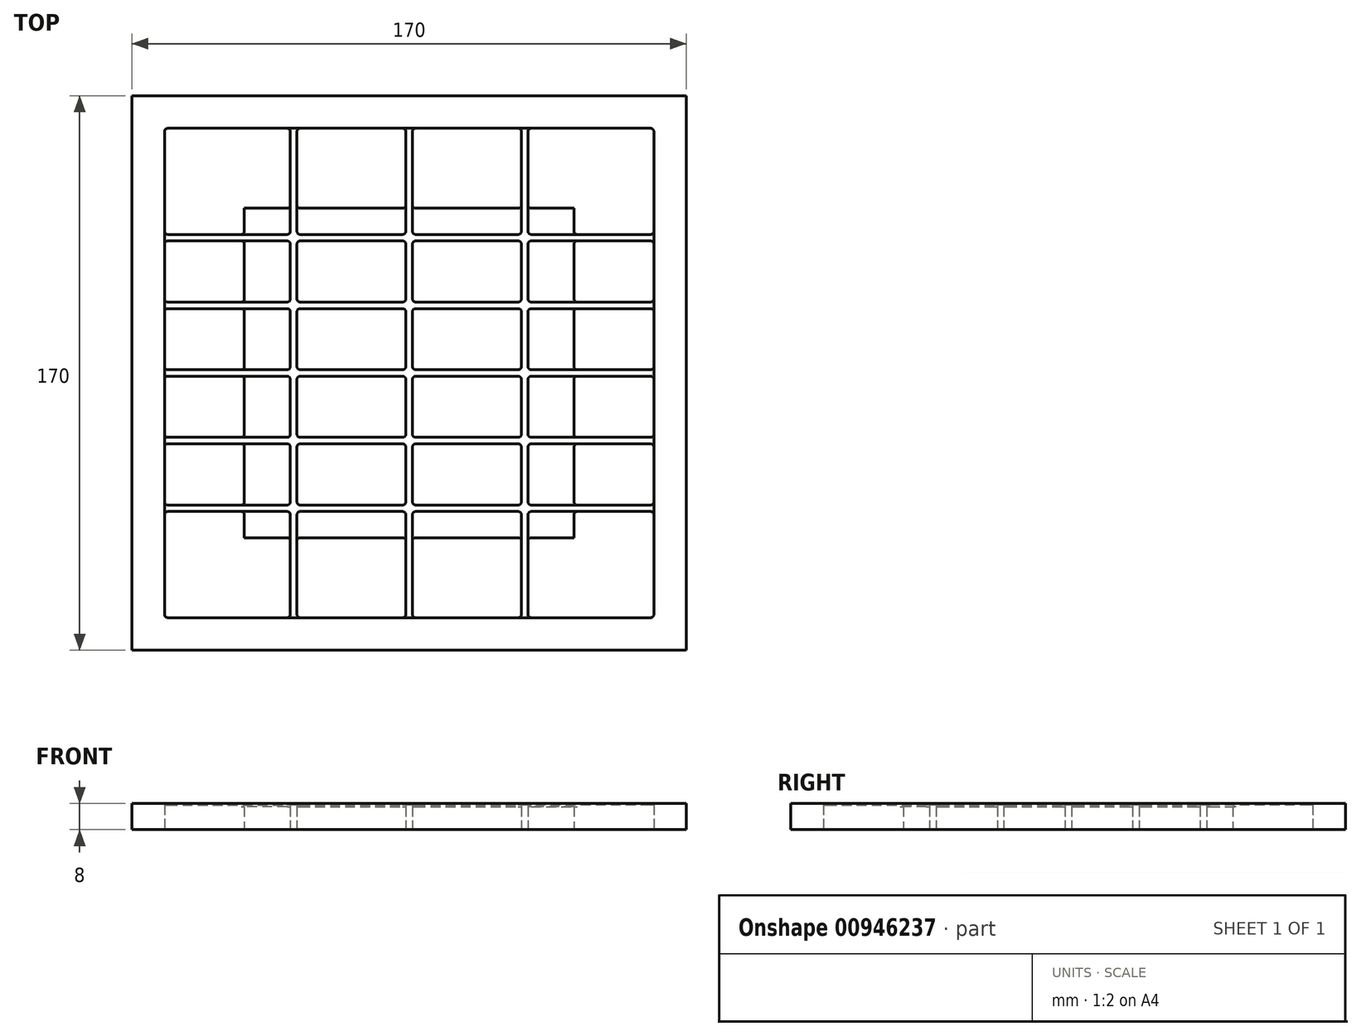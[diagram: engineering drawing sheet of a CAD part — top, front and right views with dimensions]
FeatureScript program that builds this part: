
annotation { "Feature Type Name" : "Feature", "Feature Type Description" : "" }
export const myFeature = defineFeature(function(context is Context, id is Id, definition is map)
    precondition{}
    {
        {
            var Q0;
            Q0=qCreatedBy(makeId("Top.planeOp"),FACE);
            var sketch = newSketch(context, id + "F0", { "sketchPlane" : qUnion([Q0])});
            skLineSegment(sketch, "E0", {"start": v(-85, -85) * mm, "end": v(-85, 85) * mm});
            skLineSegment(sketch, "E1", {"start": v(-85, 85) * mm, "end": v(85, 85) * mm});
            skLineSegment(sketch, "E2", {"start": v(85, 85) * mm, "end": v(85, -85) * mm});
            skLineSegment(sketch, "E3", {"start": v(85, -85) * mm, "end": v(-85, -85) * mm});
            skLineSegment(sketch, "E4", {"start": v(-2, -21.74) * mm, "end": v(-33.4, -21.74) * mm});
            skArc(sketch, "E5", {"start": v(-33.4, -21.74) * mm, "mid": v(-34.12, -22.03) * mm, "end": v(-34.4, -22.74) * mm});
            skLineSegment(sketch, "E6", {"start": v(-34.4, -22.74) * mm, "end": v(-34.4, -39.47) * mm});
            skArc(sketch, "E7", {"start": v(-34.4, -39.47) * mm, "mid": v(-34.12, -40.18) * mm, "end": v(-33.4, -40.47) * mm});
            skLineSegment(sketch, "E8", {"start": v(-33.4, -40.47) * mm, "end": v(-2, -40.47) * mm});
            skArc(sketch, "E9", {"start": v(-2, -40.47) * mm, "mid": v(-1.3, -40.18) * mm, "end": v(-1, -39.47) * mm});
            skLineSegment(sketch, "E10", {"start": v(-1, -39.47) * mm, "end": v(-1, -22.74) * mm});
            skArc(sketch, "E11", {"start": v(-1, -22.74) * mm, "mid": v(-1.3, -22.03) * mm, "end": v(-2, -21.74) * mm});
            skLineSegment(sketch, "E12", {"start": v(-2, 40.47) * mm, "end": v(-33.4, 40.47) * mm});
            skArc(sketch, "E13", {"start": v(-33.4, 40.47) * mm, "mid": v(-34.12, 40.18) * mm, "end": v(-34.4, 39.47) * mm});
            skLineSegment(sketch, "E14", {"start": v(-34.4, 39.47) * mm, "end": v(-34.4, 22.73) * mm});
            skArc(sketch, "E15", {"start": v(-34.4, 22.73) * mm, "mid": v(-34.12, 22.03) * mm, "end": v(-33.4, 21.73) * mm});
            skLineSegment(sketch, "E16", {"start": v(-33.4, 21.73) * mm, "end": v(-2, 21.73) * mm});
            skArc(sketch, "E17", {"start": v(-2, 21.73) * mm, "mid": v(-1.3, 22.03) * mm, "end": v(-1, 22.73) * mm});
            skLineSegment(sketch, "E18", {"start": v(-1, 22.73) * mm, "end": v(-1, 39.47) * mm});
            skArc(sketch, "E19", {"start": v(-1, 39.47) * mm, "mid": v(-1.3, 40.18) * mm, "end": v(-2, 40.47) * mm});
            skArc(sketch, "E20", {"start": v(1, 22.73) * mm, "mid": v(1.3, 22.03) * mm, "end": v(2, 21.73) * mm});
            skLineSegment(sketch, "E21", {"start": v(2, 21.73) * mm, "end": v(33.4, 21.73) * mm});
            skArc(sketch, "E22", {"start": v(33.4, 21.73) * mm, "mid": v(34.12, 22.03) * mm, "end": v(34.4, 22.73) * mm});
            skLineSegment(sketch, "E23", {"start": v(34.4, 22.73) * mm, "end": v(34.4, 39.47) * mm});
            skArc(sketch, "E24", {"start": v(34.4, 39.47) * mm, "mid": v(34.12, 40.18) * mm, "end": v(33.4, 40.47) * mm});
            skLineSegment(sketch, "E25", {"start": v(33.4, 40.47) * mm, "end": v(2, 40.47) * mm});
            skArc(sketch, "E26", {"start": v(2, 40.47) * mm, "mid": v(1.3, 40.18) * mm, "end": v(1, 39.47) * mm});
            skLineSegment(sketch, "E27", {"start": v(1, 39.47) * mm, "end": v(1, 22.73) * mm});
            skLineSegment(sketch, "E28", {"start": v(-33.4, 1) * mm, "end": v(-2, 1) * mm});
            skArc(sketch, "E29", {"start": v(-2, 1) * mm, "mid": v(-1.3, 1.3) * mm, "end": v(-1, 2) * mm});
            skLineSegment(sketch, "E30", {"start": v(-1, 2) * mm, "end": v(-1, 18.73) * mm});
            skArc(sketch, "E31", {"start": v(-1, 18.73) * mm, "mid": v(-1.3, 19.44) * mm, "end": v(-2, 19.73) * mm});
            skLineSegment(sketch, "E32", {"start": v(-2, 19.73) * mm, "end": v(-33.4, 19.73) * mm});
            skArc(sketch, "E33", {"start": v(-33.4, 19.73) * mm, "mid": v(-34.12, 19.44) * mm, "end": v(-34.4, 18.73) * mm});
            skLineSegment(sketch, "E34", {"start": v(-34.4, 18.73) * mm, "end": v(-34.4, 2) * mm});
            skArc(sketch, "E35", {"start": v(-34.4, 2) * mm, "mid": v(-34.12, 1.3) * mm, "end": v(-33.4, 1) * mm});
            skLineSegment(sketch, "E36", {"start": v(2, 1) * mm, "end": v(33.4, 1) * mm});
            skArc(sketch, "E37", {"start": v(33.4, 1) * mm, "mid": v(34.12, 1.3) * mm, "end": v(34.4, 2) * mm});
            skLineSegment(sketch, "E38", {"start": v(34.4, 2) * mm, "end": v(34.4, 18.73) * mm});
            skArc(sketch, "E39", {"start": v(34.4, 18.73) * mm, "mid": v(34.12, 19.44) * mm, "end": v(33.4, 19.73) * mm});
            skLineSegment(sketch, "E40", {"start": v(33.4, 19.73) * mm, "end": v(2, 19.73) * mm});
            skArc(sketch, "E41", {"start": v(2, 19.73) * mm, "mid": v(1.3, 19.44) * mm, "end": v(1, 18.73) * mm});
            skLineSegment(sketch, "E42", {"start": v(1, 18.73) * mm, "end": v(1, 2) * mm});
            skArc(sketch, "E43", {"start": v(1, 2) * mm, "mid": v(1.3, 1.3) * mm, "end": v(2, 1) * mm});
            skArc(sketch, "E44", {"start": v(33.4, -19.74) * mm, "mid": v(34.12, -19.44) * mm, "end": v(34.4, -18.74) * mm});
            skLineSegment(sketch, "E45", {"start": v(34.4, -18.74) * mm, "end": v(34.4, -2) * mm});
            skArc(sketch, "E46", {"start": v(34.4, -2) * mm, "mid": v(34.12, -1.3) * mm, "end": v(33.4, -1) * mm});
            skLineSegment(sketch, "E47", {"start": v(33.4, -1) * mm, "end": v(2, -1) * mm});
            skArc(sketch, "E48", {"start": v(2, -1) * mm, "mid": v(1.3, -1.3) * mm, "end": v(1, -2) * mm});
            skLineSegment(sketch, "E49", {"start": v(1, -2) * mm, "end": v(1, -18.74) * mm});
            skArc(sketch, "E50", {"start": v(1, -18.74) * mm, "mid": v(1.3, -19.44) * mm, "end": v(2, -19.74) * mm});
            skLineSegment(sketch, "E51", {"start": v(2, -19.74) * mm, "end": v(33.4, -19.74) * mm});
            skLineSegment(sketch, "E52", {"start": v(-1, -18.74) * mm, "end": v(-1, -2) * mm});
            skArc(sketch, "E53", {"start": v(-1, -2) * mm, "mid": v(-1.3, -1.3) * mm, "end": v(-2, -1) * mm});
            skLineSegment(sketch, "E54", {"start": v(-2, -1) * mm, "end": v(-33.4, -1) * mm});
            skArc(sketch, "E55", {"start": v(-33.4, -1) * mm, "mid": v(-34.12, -1.3) * mm, "end": v(-34.4, -2) * mm});
            skLineSegment(sketch, "E56", {"start": v(-34.4, -2) * mm, "end": v(-34.4, -18.74) * mm});
            skArc(sketch, "E57", {"start": v(-34.4, -18.74) * mm, "mid": v(-34.12, -19.44) * mm, "end": v(-33.4, -19.74) * mm});
            skLineSegment(sketch, "E58", {"start": v(-33.4, -19.74) * mm, "end": v(-2, -19.74) * mm});
            skArc(sketch, "E59", {"start": v(-2, -19.74) * mm, "mid": v(-1.3, -19.44) * mm, "end": v(-1, -18.74) * mm});
            skArc(sketch, "E60", {"start": v(2, -21.74) * mm, "mid": v(1.3, -22.03) * mm, "end": v(1, -22.74) * mm});
            skLineSegment(sketch, "E61", {"start": v(1, -22.74) * mm, "end": v(1, -39.47) * mm});
            skArc(sketch, "E62", {"start": v(1, -39.47) * mm, "mid": v(1.3, -40.18) * mm, "end": v(2, -40.47) * mm});
            skLineSegment(sketch, "E63", {"start": v(2, -40.47) * mm, "end": v(33.4, -40.47) * mm});
            skArc(sketch, "E64", {"start": v(33.4, -40.47) * mm, "mid": v(34.12, -40.18) * mm, "end": v(34.4, -39.47) * mm});
            skLineSegment(sketch, "E65", {"start": v(34.4, -39.47) * mm, "end": v(34.4, -22.74) * mm});
            skArc(sketch, "E66", {"start": v(34.4, -22.74) * mm, "mid": v(34.12, -22.03) * mm, "end": v(33.4, -21.74) * mm});
            skLineSegment(sketch, "E67", {"start": v(33.4, -21.74) * mm, "end": v(2, -21.74) * mm});
            skLineSegment(sketch, "E68", {"start": v(36.4, 50.5) * mm, "end": v(36.4, 43.47) * mm});
            skArc(sketch, "E69", {"start": v(36.4, 43.47) * mm, "mid": v(36.7, 42.76) * mm, "end": v(37.4, 42.47) * mm});
            skLineSegment(sketch, "E70", {"start": v(37.4, 42.47) * mm, "end": v(50.5, 42.47) * mm});
            skLineSegment(sketch, "E71", {"start": v(50.5, 42.47) * mm, "end": v(50.5, 50.5) * mm});
            skLineSegment(sketch, "E72", {"start": v(50.5, 50.5) * mm, "end": v(36.4, 50.5) * mm});
            skLineSegment(sketch, "E73", {"start": v(1, 50.5) * mm, "end": v(1, 43.47) * mm});
            skArc(sketch, "E74", {"start": v(1, 43.47) * mm, "mid": v(1.3, 42.76) * mm, "end": v(2, 42.47) * mm});
            skLineSegment(sketch, "E75", {"start": v(2, 42.47) * mm, "end": v(33.4, 42.47) * mm});
            skArc(sketch, "E76", {"start": v(33.4, 42.47) * mm, "mid": v(34.12, 42.76) * mm, "end": v(34.4, 43.47) * mm});
            skLineSegment(sketch, "E77", {"start": v(34.4, 43.47) * mm, "end": v(34.4, 50.5) * mm});
            skLineSegment(sketch, "E78", {"start": v(34.4, 50.5) * mm, "end": v(1, 50.5) * mm});
            skLineSegment(sketch, "E79", {"start": v(-34.4, 50.5) * mm, "end": v(-34.4, 43.47) * mm});
            skArc(sketch, "E80", {"start": v(-34.4, 43.47) * mm, "mid": v(-34.12, 42.76) * mm, "end": v(-33.4, 42.47) * mm});
            skLineSegment(sketch, "E81", {"start": v(-33.4, 42.47) * mm, "end": v(-2, 42.47) * mm});
            skArc(sketch, "E82", {"start": v(-2, 42.47) * mm, "mid": v(-1.3, 42.76) * mm, "end": v(-1, 43.47) * mm});
            skLineSegment(sketch, "E83", {"start": v(-1, 43.47) * mm, "end": v(-1, 50.5) * mm});
            skLineSegment(sketch, "E84", {"start": v(-1, 50.5) * mm, "end": v(-34.4, 50.5) * mm});
            skLineSegment(sketch, "E85", {"start": v(-50.5, -40.47) * mm, "end": v(-37.4, -40.47) * mm});
            skArc(sketch, "E86", {"start": v(-37.4, -40.47) * mm, "mid": v(-36.7, -40.18) * mm, "end": v(-36.4, -39.47) * mm});
            skLineSegment(sketch, "E87", {"start": v(-36.4, -39.47) * mm, "end": v(-36.4, -22.74) * mm});
            skArc(sketch, "E88", {"start": v(-36.4, -22.74) * mm, "mid": v(-36.7, -22.03) * mm, "end": v(-37.4, -21.74) * mm});
            skLineSegment(sketch, "E89", {"start": v(-37.4, -21.74) * mm, "end": v(-50.5, -21.74) * mm});
            skLineSegment(sketch, "E90", {"start": v(-50.5, -21.74) * mm, "end": v(-50.5, -40.47) * mm});
            skLineSegment(sketch, "E91", {"start": v(-50.5, -19.74) * mm, "end": v(-37.4, -19.74) * mm});
            skArc(sketch, "E92", {"start": v(-37.4, -19.74) * mm, "mid": v(-36.7, -19.44) * mm, "end": v(-36.4, -18.74) * mm});
            skLineSegment(sketch, "E93", {"start": v(-36.4, -18.74) * mm, "end": v(-36.4, -2) * mm});
            skArc(sketch, "E94", {"start": v(-36.4, -2) * mm, "mid": v(-36.7, -1.3) * mm, "end": v(-37.4, -1) * mm});
            skLineSegment(sketch, "E95", {"start": v(-37.4, -1) * mm, "end": v(-50.5, -1) * mm});
            skLineSegment(sketch, "E96", {"start": v(-50.5, -1) * mm, "end": v(-50.5, -19.74) * mm});
            skLineSegment(sketch, "E97", {"start": v(-50.5, 1) * mm, "end": v(-37.4, 1) * mm});
            skArc(sketch, "E98", {"start": v(-37.4, 1) * mm, "mid": v(-36.7, 1.3) * mm, "end": v(-36.4, 2) * mm});
            skLineSegment(sketch, "E99", {"start": v(-36.4, 2) * mm, "end": v(-36.4, 18.73) * mm});
            skArc(sketch, "E100", {"start": v(-36.4, 18.73) * mm, "mid": v(-36.7, 19.44) * mm, "end": v(-37.4, 19.73) * mm});
            skLineSegment(sketch, "E101", {"start": v(-37.4, 19.73) * mm, "end": v(-50.5, 19.73) * mm});
            skLineSegment(sketch, "E102", {"start": v(-50.5, 19.73) * mm, "end": v(-50.5, 1) * mm});
            skLineSegment(sketch, "E103", {"start": v(-50.5, 21.73) * mm, "end": v(-37.4, 21.73) * mm});
            skArc(sketch, "E104", {"start": v(-37.4, 21.73) * mm, "mid": v(-36.7, 22.03) * mm, "end": v(-36.4, 22.73) * mm});
            skLineSegment(sketch, "E105", {"start": v(-36.4, 22.73) * mm, "end": v(-36.4, 39.47) * mm});
            skArc(sketch, "E106", {"start": v(-36.4, 39.47) * mm, "mid": v(-36.7, 40.18) * mm, "end": v(-37.4, 40.47) * mm});
            skLineSegment(sketch, "E107", {"start": v(-37.4, 40.47) * mm, "end": v(-50.5, 40.47) * mm});
            skLineSegment(sketch, "E108", {"start": v(-50.5, 40.47) * mm, "end": v(-50.5, 21.73) * mm});
            skLineSegment(sketch, "E109", {"start": v(-50.5, 42.47) * mm, "end": v(-37.4, 42.47) * mm});
            skArc(sketch, "E110", {"start": v(-37.4, 42.47) * mm, "mid": v(-36.7, 42.76) * mm, "end": v(-36.4, 43.47) * mm});
            skLineSegment(sketch, "E111", {"start": v(-36.4, 43.47) * mm, "end": v(-36.4, 50.5) * mm});
            skLineSegment(sketch, "E112", {"start": v(-36.4, 50.5) * mm, "end": v(-50.5, 50.5) * mm});
            skLineSegment(sketch, "E113", {"start": v(-50.5, 50.5) * mm, "end": v(-50.5, 42.47) * mm});
            skLineSegment(sketch, "E114", {"start": v(34.4, -50.5) * mm, "end": v(34.4, -43.47) * mm});
            skArc(sketch, "E115", {"start": v(34.4, -43.47) * mm, "mid": v(34.12, -42.76) * mm, "end": v(33.4, -42.47) * mm});
            skLineSegment(sketch, "E116", {"start": v(33.4, -42.47) * mm, "end": v(2, -42.47) * mm});
            skArc(sketch, "E117", {"start": v(2, -42.47) * mm, "mid": v(1.3, -42.76) * mm, "end": v(1, -43.47) * mm});
            skLineSegment(sketch, "E118", {"start": v(1, -43.47) * mm, "end": v(1, -50.5) * mm});
            skLineSegment(sketch, "E119", {"start": v(1, -50.5) * mm, "end": v(34.4, -50.5) * mm});
            skLineSegment(sketch, "E120", {"start": v(-1, -50.5) * mm, "end": v(-1, -43.47) * mm});
            skArc(sketch, "E121", {"start": v(-1, -43.47) * mm, "mid": v(-1.3, -42.76) * mm, "end": v(-2, -42.47) * mm});
            skLineSegment(sketch, "E122", {"start": v(-2, -42.47) * mm, "end": v(-33.4, -42.47) * mm});
            skArc(sketch, "E123", {"start": v(-33.4, -42.47) * mm, "mid": v(-34.12, -42.76) * mm, "end": v(-34.4, -43.47) * mm});
            skLineSegment(sketch, "E124", {"start": v(-34.4, -43.47) * mm, "end": v(-34.4, -50.5) * mm});
            skLineSegment(sketch, "E125", {"start": v(-34.4, -50.5) * mm, "end": v(-1, -50.5) * mm});
            skLineSegment(sketch, "E126", {"start": v(-36.4, -50.5) * mm, "end": v(-36.4, -43.47) * mm});
            skArc(sketch, "E127", {"start": v(-36.4, -43.47) * mm, "mid": v(-36.7, -42.76) * mm, "end": v(-37.4, -42.47) * mm});
            skLineSegment(sketch, "E128", {"start": v(-37.4, -42.47) * mm, "end": v(-50.5, -42.47) * mm});
            skLineSegment(sketch, "E129", {"start": v(-50.5, -42.47) * mm, "end": v(-50.5, -50.5) * mm});
            skLineSegment(sketch, "E130", {"start": v(-50.5, -50.5) * mm, "end": v(-36.4, -50.5) * mm});
            skLineSegment(sketch, "E131", {"start": v(50.5, -42.47) * mm, "end": v(37.4, -42.47) * mm});
            skArc(sketch, "E132", {"start": v(37.4, -42.47) * mm, "mid": v(36.7, -42.76) * mm, "end": v(36.4, -43.47) * mm});
            skLineSegment(sketch, "E133", {"start": v(36.4, -43.47) * mm, "end": v(36.4, -50.5) * mm});
            skLineSegment(sketch, "E134", {"start": v(36.4, -50.5) * mm, "end": v(50.5, -50.5) * mm});
            skLineSegment(sketch, "E135", {"start": v(50.5, -50.5) * mm, "end": v(50.5, -42.47) * mm});
            skLineSegment(sketch, "E136", {"start": v(50.5, -21.74) * mm, "end": v(37.4, -21.74) * mm});
            skArc(sketch, "E137", {"start": v(37.4, -21.74) * mm, "mid": v(36.7, -22.03) * mm, "end": v(36.4, -22.74) * mm});
            skLineSegment(sketch, "E138", {"start": v(36.4, -22.74) * mm, "end": v(36.4, -39.47) * mm});
            skArc(sketch, "E139", {"start": v(36.4, -39.47) * mm, "mid": v(36.7, -40.18) * mm, "end": v(37.4, -40.47) * mm});
            skLineSegment(sketch, "E140", {"start": v(37.4, -40.47) * mm, "end": v(50.5, -40.47) * mm});
            skLineSegment(sketch, "E141", {"start": v(50.5, -40.47) * mm, "end": v(50.5, -21.74) * mm});
            skLineSegment(sketch, "E142", {"start": v(50.5, -1) * mm, "end": v(37.4, -1) * mm});
            skArc(sketch, "E143", {"start": v(37.4, -1) * mm, "mid": v(36.7, -1.3) * mm, "end": v(36.4, -2) * mm});
            skLineSegment(sketch, "E144", {"start": v(36.4, -2) * mm, "end": v(36.4, -18.74) * mm});
            skArc(sketch, "E145", {"start": v(36.4, -18.74) * mm, "mid": v(36.7, -19.44) * mm, "end": v(37.4, -19.74) * mm});
            skLineSegment(sketch, "E146", {"start": v(37.4, -19.74) * mm, "end": v(50.5, -19.74) * mm});
            skLineSegment(sketch, "E147", {"start": v(50.5, -19.74) * mm, "end": v(50.5, -1) * mm});
            skLineSegment(sketch, "E148", {"start": v(50.5, 19.73) * mm, "end": v(37.4, 19.73) * mm});
            skArc(sketch, "E149", {"start": v(37.4, 19.73) * mm, "mid": v(36.7, 19.44) * mm, "end": v(36.4, 18.73) * mm});
            skLineSegment(sketch, "E150", {"start": v(36.4, 18.73) * mm, "end": v(36.4, 2) * mm});
            skArc(sketch, "E151", {"start": v(36.4, 2) * mm, "mid": v(36.7, 1.3) * mm, "end": v(37.4, 1) * mm});
            skLineSegment(sketch, "E152", {"start": v(37.4, 1) * mm, "end": v(50.5, 1) * mm});
            skLineSegment(sketch, "E153", {"start": v(50.5, 1) * mm, "end": v(50.5, 19.73) * mm});
            skLineSegment(sketch, "E154", {"start": v(50.5, 40.47) * mm, "end": v(37.4, 40.47) * mm});
            skArc(sketch, "E155", {"start": v(37.4, 40.47) * mm, "mid": v(36.7, 40.18) * mm, "end": v(36.4, 39.47) * mm});
            skLineSegment(sketch, "E156", {"start": v(36.4, 39.47) * mm, "end": v(36.4, 22.73) * mm});
            skArc(sketch, "E157", {"start": v(36.4, 22.73) * mm, "mid": v(36.7, 22.03) * mm, "end": v(37.4, 21.73) * mm});
            skLineSegment(sketch, "E158", {"start": v(37.4, 21.73) * mm, "end": v(50.5, 21.73) * mm});
            skLineSegment(sketch, "E159", {"start": v(50.5, 21.73) * mm, "end": v(50.5, 40.47) * mm});
            skArc(sketch, "E160", {"start": v(75, 2) * mm, "mid": v(74.7, 1.3) * mm, "end": v(74, 1) * mm});
            skLineSegment(sketch, "E161", {"start": v(74, 1) * mm, "end": v(37.4, 1) * mm});
            skArc(sketch, "E162", {"start": v(37.4, 1) * mm, "mid": v(36.7, 1.3) * mm, "end": v(36.4, 2) * mm});
            skLineSegment(sketch, "E163", {"start": v(36.4, 2) * mm, "end": v(36.4, 18.73) * mm});
            skArc(sketch, "E164", {"start": v(36.4, 18.73) * mm, "mid": v(36.7, 19.44) * mm, "end": v(37.4, 19.73) * mm});
            skLineSegment(sketch, "E165", {"start": v(37.4, 19.73) * mm, "end": v(74, 19.73) * mm});
            skArc(sketch, "E166", {"start": v(74, 19.73) * mm, "mid": v(74.7, 19.44) * mm, "end": v(75, 18.73) * mm});
            skLineSegment(sketch, "E167", {"start": v(75, 18.73) * mm, "end": v(75, 22.73) * mm});
            skArc(sketch, "E168", {"start": v(75, 22.73) * mm, "mid": v(74.7, 22.03) * mm, "end": v(74, 21.73) * mm});
            skLineSegment(sketch, "E169", {"start": v(74, 21.73) * mm, "end": v(37.4, 21.73) * mm});
            skArc(sketch, "E170", {"start": v(37.4, 21.73) * mm, "mid": v(36.7, 22.03) * mm, "end": v(36.4, 22.73) * mm});
            skLineSegment(sketch, "E171", {"start": v(36.4, 22.73) * mm, "end": v(36.4, 39.47) * mm});
            skArc(sketch, "E172", {"start": v(36.4, 39.47) * mm, "mid": v(36.7, 40.18) * mm, "end": v(37.4, 40.47) * mm});
            skLineSegment(sketch, "E173", {"start": v(37.4, 40.47) * mm, "end": v(74, 40.47) * mm});
            skArc(sketch, "E174", {"start": v(74, 40.47) * mm, "mid": v(74.7, 40.18) * mm, "end": v(75, 39.47) * mm});
            skLineSegment(sketch, "E175", {"start": v(75, 39.47) * mm, "end": v(75, 43.47) * mm});
            skArc(sketch, "E176", {"start": v(75, 43.47) * mm, "mid": v(74.7, 42.76) * mm, "end": v(74, 42.47) * mm});
            skLineSegment(sketch, "E177", {"start": v(74, 42.47) * mm, "end": v(37.4, 42.47) * mm});
            skArc(sketch, "E178", {"start": v(37.4, 42.47) * mm, "mid": v(36.7, 42.76) * mm, "end": v(36.4, 43.47) * mm});
            skLineSegment(sketch, "E179", {"start": v(36.4, 43.47) * mm, "end": v(36.4, 74) * mm});
            skArc(sketch, "E180", {"start": v(36.4, 74) * mm, "mid": v(36.7, 74.7) * mm, "end": v(37.4, 75) * mm});
            skLineSegment(sketch, "E181", {"start": v(37.4, 75) * mm, "end": v(33.4, 75) * mm});
            skArc(sketch, "E182", {"start": v(33.4, 75) * mm, "mid": v(34.12, 74.7) * mm, "end": v(34.4, 74) * mm});
            skLineSegment(sketch, "E183", {"start": v(34.4, 74) * mm, "end": v(34.4, 43.47) * mm});
            skArc(sketch, "E184", {"start": v(34.4, 43.47) * mm, "mid": v(34.12, 42.76) * mm, "end": v(33.4, 42.47) * mm});
            skLineSegment(sketch, "E185", {"start": v(33.4, 42.47) * mm, "end": v(2, 42.47) * mm});
            skArc(sketch, "E186", {"start": v(2, 42.47) * mm, "mid": v(1.3, 42.76) * mm, "end": v(1, 43.47) * mm});
            skLineSegment(sketch, "E187", {"start": v(1, 43.47) * mm, "end": v(1, 74) * mm});
            skArc(sketch, "E188", {"start": v(1, 74) * mm, "mid": v(1.3, 74.7) * mm, "end": v(2, 75) * mm});
            skLineSegment(sketch, "E189", {"start": v(2, 75) * mm, "end": v(-2, 75) * mm});
            skArc(sketch, "E190", {"start": v(-2, 75) * mm, "mid": v(-1.3, 74.7) * mm, "end": v(-1, 74) * mm});
            skLineSegment(sketch, "E191", {"start": v(-1, 74) * mm, "end": v(-1, 43.47) * mm});
            skArc(sketch, "E192", {"start": v(-1, 43.47) * mm, "mid": v(-1.3, 42.76) * mm, "end": v(-2, 42.47) * mm});
            skLineSegment(sketch, "E193", {"start": v(-2, 42.47) * mm, "end": v(-33.4, 42.47) * mm});
            skArc(sketch, "E194", {"start": v(-33.4, 42.47) * mm, "mid": v(-34.12, 42.76) * mm, "end": v(-34.4, 43.47) * mm});
            skLineSegment(sketch, "E195", {"start": v(-34.4, 43.47) * mm, "end": v(-34.4, 74) * mm});
            skArc(sketch, "E196", {"start": v(-34.4, 74) * mm, "mid": v(-34.12, 74.7) * mm, "end": v(-33.4, 75) * mm});
            skLineSegment(sketch, "E197", {"start": v(-33.4, 75) * mm, "end": v(-37.4, 75) * mm});
            skArc(sketch, "E198", {"start": v(-37.4, 75) * mm, "mid": v(-36.7, 74.7) * mm, "end": v(-36.4, 74) * mm});
            skLineSegment(sketch, "E199", {"start": v(-36.4, 74) * mm, "end": v(-36.4, 43.47) * mm});
            skArc(sketch, "E200", {"start": v(-36.4, 43.47) * mm, "mid": v(-36.7, 42.76) * mm, "end": v(-37.4, 42.47) * mm});
            skLineSegment(sketch, "E201", {"start": v(-37.4, 42.47) * mm, "end": v(-74, 42.47) * mm});
            skArc(sketch, "E202", {"start": v(-74, 42.47) * mm, "mid": v(-74.7, 42.76) * mm, "end": v(-75, 43.47) * mm});
            skLineSegment(sketch, "E203", {"start": v(-75, 43.47) * mm, "end": v(-75, 39.47) * mm});
            skArc(sketch, "E204", {"start": v(-75, 39.47) * mm, "mid": v(-74.7, 40.18) * mm, "end": v(-74, 40.47) * mm});
            skLineSegment(sketch, "E205", {"start": v(-74, 40.47) * mm, "end": v(-37.4, 40.47) * mm});
            skArc(sketch, "E206", {"start": v(-37.4, 40.47) * mm, "mid": v(-36.7, 40.18) * mm, "end": v(-36.4, 39.47) * mm});
            skLineSegment(sketch, "E207", {"start": v(-36.4, 39.47) * mm, "end": v(-36.4, 22.73) * mm});
            skArc(sketch, "E208", {"start": v(-36.4, 22.73) * mm, "mid": v(-36.7, 22.03) * mm, "end": v(-37.4, 21.73) * mm});
            skLineSegment(sketch, "E209", {"start": v(-37.4, 21.73) * mm, "end": v(-74, 21.73) * mm});
            skArc(sketch, "E210", {"start": v(-74, 21.73) * mm, "mid": v(-74.7, 22.03) * mm, "end": v(-75, 22.73) * mm});
            skLineSegment(sketch, "E211", {"start": v(-75, 22.73) * mm, "end": v(-75, 18.73) * mm});
            skArc(sketch, "E212", {"start": v(-75, 18.73) * mm, "mid": v(-74.7, 19.44) * mm, "end": v(-74, 19.73) * mm});
            skLineSegment(sketch, "E213", {"start": v(-74, 19.73) * mm, "end": v(-37.4, 19.73) * mm});
            skArc(sketch, "E214", {"start": v(-37.4, 19.73) * mm, "mid": v(-36.7, 19.44) * mm, "end": v(-36.4, 18.73) * mm});
            skLineSegment(sketch, "E215", {"start": v(-36.4, 18.73) * mm, "end": v(-36.4, 2) * mm});
            skArc(sketch, "E216", {"start": v(-36.4, 2) * mm, "mid": v(-36.7, 1.3) * mm, "end": v(-37.4, 1) * mm});
            skLineSegment(sketch, "E217", {"start": v(-37.4, 1) * mm, "end": v(-74, 1) * mm});
            skArc(sketch, "E218", {"start": v(-74, 1) * mm, "mid": v(-74.7, 1.3) * mm, "end": v(-75, 2) * mm});
            skLineSegment(sketch, "E219", {"start": v(-75, 2) * mm, "end": v(-75, -2) * mm});
            skArc(sketch, "E220", {"start": v(-75, -2) * mm, "mid": v(-74.7, -1.3) * mm, "end": v(-74, -1) * mm});
            skLineSegment(sketch, "E221", {"start": v(-74, -1) * mm, "end": v(-37.4, -1) * mm});
            skArc(sketch, "E222", {"start": v(-37.4, -1) * mm, "mid": v(-36.7, -1.3) * mm, "end": v(-36.4, -2) * mm});
            skLineSegment(sketch, "E223", {"start": v(-36.4, -2) * mm, "end": v(-36.4, -18.74) * mm});
            skArc(sketch, "E224", {"start": v(-36.4, -18.74) * mm, "mid": v(-36.7, -19.44) * mm, "end": v(-37.4, -19.74) * mm});
            skLineSegment(sketch, "E225", {"start": v(-37.4, -19.74) * mm, "end": v(-74, -19.74) * mm});
            skArc(sketch, "E226", {"start": v(-74, -19.74) * mm, "mid": v(-74.7, -19.44) * mm, "end": v(-75, -18.74) * mm});
            skLineSegment(sketch, "E227", {"start": v(-75, -18.74) * mm, "end": v(-75, -22.74) * mm});
            skArc(sketch, "E228", {"start": v(-75, -22.74) * mm, "mid": v(-74.7, -22.03) * mm, "end": v(-74, -21.74) * mm});
            skLineSegment(sketch, "E229", {"start": v(-74, -21.74) * mm, "end": v(-37.4, -21.74) * mm});
            skArc(sketch, "E230", {"start": v(-37.4, -21.74) * mm, "mid": v(-36.7, -22.03) * mm, "end": v(-36.4, -22.74) * mm});
            skLineSegment(sketch, "E231", {"start": v(-36.4, -22.74) * mm, "end": v(-36.4, -39.47) * mm});
            skArc(sketch, "E232", {"start": v(-36.4, -39.47) * mm, "mid": v(-36.7, -40.18) * mm, "end": v(-37.4, -40.47) * mm});
            skLineSegment(sketch, "E233", {"start": v(-37.4, -40.47) * mm, "end": v(-74, -40.47) * mm});
            skArc(sketch, "E234", {"start": v(-74, -40.47) * mm, "mid": v(-74.7, -40.18) * mm, "end": v(-75, -39.47) * mm});
            skLineSegment(sketch, "E235", {"start": v(-75, -39.47) * mm, "end": v(-75, -43.47) * mm});
            skArc(sketch, "E236", {"start": v(-75, -43.47) * mm, "mid": v(-74.7, -42.76) * mm, "end": v(-74, -42.47) * mm});
            skLineSegment(sketch, "E237", {"start": v(-74, -42.47) * mm, "end": v(-37.4, -42.47) * mm});
            skArc(sketch, "E238", {"start": v(-37.4, -42.47) * mm, "mid": v(-36.7, -42.76) * mm, "end": v(-36.4, -43.47) * mm});
            skLineSegment(sketch, "E239", {"start": v(-36.4, -43.47) * mm, "end": v(-36.4, -74) * mm});
            skArc(sketch, "E240", {"start": v(-36.4, -74) * mm, "mid": v(-36.7, -74.7) * mm, "end": v(-37.4, -75) * mm});
            skLineSegment(sketch, "E241", {"start": v(-37.4, -75) * mm, "end": v(-33.4, -75) * mm});
            skArc(sketch, "E242", {"start": v(-33.4, -75) * mm, "mid": v(-34.12, -74.7) * mm, "end": v(-34.4, -74) * mm});
            skLineSegment(sketch, "E243", {"start": v(-34.4, -74) * mm, "end": v(-34.4, -43.47) * mm});
            skArc(sketch, "E244", {"start": v(-34.4, -43.47) * mm, "mid": v(-34.12, -42.76) * mm, "end": v(-33.4, -42.47) * mm});
            skLineSegment(sketch, "E245", {"start": v(-33.4, -42.47) * mm, "end": v(-2, -42.47) * mm});
            skArc(sketch, "E246", {"start": v(-2, -42.47) * mm, "mid": v(-1.3, -42.76) * mm, "end": v(-1, -43.47) * mm});
            skLineSegment(sketch, "E247", {"start": v(-1, -43.47) * mm, "end": v(-1, -74) * mm});
            skArc(sketch, "E248", {"start": v(-1, -74) * mm, "mid": v(-1.3, -74.7) * mm, "end": v(-2, -75) * mm});
            skLineSegment(sketch, "E249", {"start": v(-2, -75) * mm, "end": v(2, -75) * mm});
            skArc(sketch, "E250", {"start": v(2, -75) * mm, "mid": v(1.3, -74.7) * mm, "end": v(1, -74) * mm});
            skLineSegment(sketch, "E251", {"start": v(1, -74) * mm, "end": v(1, -43.47) * mm});
            skArc(sketch, "E252", {"start": v(1, -43.47) * mm, "mid": v(1.3, -42.76) * mm, "end": v(2, -42.47) * mm});
            skLineSegment(sketch, "E253", {"start": v(2, -42.47) * mm, "end": v(33.4, -42.47) * mm});
            skArc(sketch, "E254", {"start": v(33.4, -42.47) * mm, "mid": v(34.12, -42.76) * mm, "end": v(34.4, -43.47) * mm});
            skLineSegment(sketch, "E255", {"start": v(34.4, -43.47) * mm, "end": v(34.4, -74) * mm});
            skArc(sketch, "E256", {"start": v(34.4, -74) * mm, "mid": v(34.12, -74.7) * mm, "end": v(33.4, -75) * mm});
            skLineSegment(sketch, "E257", {"start": v(33.4, -75) * mm, "end": v(37.4, -75) * mm});
            skArc(sketch, "E258", {"start": v(37.4, -75) * mm, "mid": v(36.7, -74.7) * mm, "end": v(36.4, -74) * mm});
            skLineSegment(sketch, "E259", {"start": v(36.4, -74) * mm, "end": v(36.4, -43.47) * mm});
            skArc(sketch, "E260", {"start": v(36.4, -43.47) * mm, "mid": v(36.7, -42.76) * mm, "end": v(37.4, -42.47) * mm});
            skLineSegment(sketch, "E261", {"start": v(37.4, -42.47) * mm, "end": v(74, -42.47) * mm});
            skArc(sketch, "E262", {"start": v(74, -42.47) * mm, "mid": v(74.7, -42.76) * mm, "end": v(75, -43.47) * mm});
            skLineSegment(sketch, "E263", {"start": v(75, -43.47) * mm, "end": v(75, -39.47) * mm});
            skArc(sketch, "E264", {"start": v(75, -39.47) * mm, "mid": v(74.7, -40.18) * mm, "end": v(74, -40.47) * mm});
            skLineSegment(sketch, "E265", {"start": v(74, -40.47) * mm, "end": v(37.4, -40.47) * mm});
            skArc(sketch, "E266", {"start": v(37.4, -40.47) * mm, "mid": v(36.7, -40.18) * mm, "end": v(36.4, -39.47) * mm});
            skLineSegment(sketch, "E267", {"start": v(36.4, -39.47) * mm, "end": v(36.4, -22.74) * mm});
            skArc(sketch, "E268", {"start": v(36.4, -22.74) * mm, "mid": v(36.7, -22.03) * mm, "end": v(37.4, -21.74) * mm});
            skLineSegment(sketch, "E269", {"start": v(37.4, -21.74) * mm, "end": v(74, -21.74) * mm});
            skArc(sketch, "E270", {"start": v(74, -21.74) * mm, "mid": v(74.7, -22.03) * mm, "end": v(75, -22.74) * mm});
            skLineSegment(sketch, "E271", {"start": v(75, -22.74) * mm, "end": v(75, -18.74) * mm});
            skArc(sketch, "E272", {"start": v(75, -18.74) * mm, "mid": v(74.7, -19.44) * mm, "end": v(74, -19.74) * mm});
            skLineSegment(sketch, "E273", {"start": v(74, -19.74) * mm, "end": v(37.4, -19.74) * mm});
            skArc(sketch, "E274", {"start": v(37.4, -19.74) * mm, "mid": v(36.7, -19.44) * mm, "end": v(36.4, -18.74) * mm});
            skLineSegment(sketch, "E275", {"start": v(36.4, -18.74) * mm, "end": v(36.4, -2) * mm});
            skArc(sketch, "E276", {"start": v(36.4, -2) * mm, "mid": v(36.7, -1.3) * mm, "end": v(37.4, -1) * mm});
            skLineSegment(sketch, "E277", {"start": v(37.4, -1) * mm, "end": v(74, -1) * mm});
            skArc(sketch, "E278", {"start": v(74, -1) * mm, "mid": v(74.7, -1.3) * mm, "end": v(75, -2) * mm});
            skLineSegment(sketch, "E279", {"start": v(75, -2) * mm, "end": v(75, 2) * mm});
            skLineSegment(sketch, "E280", {"start": v(-50.5, -18.74) * mm, "end": v(-50.5, -2) * mm});
            skArc(sketch, "E281", {"start": v(-50.5, -2) * mm, "mid": v(-50.8, -1.3) * mm, "end": v(-51.5, -1) * mm});
            skLineSegment(sketch, "E282", {"start": v(-51.5, -1) * mm, "end": v(-74, -1) * mm});
            skArc(sketch, "E283", {"start": v(-74, -1) * mm, "mid": v(-74.7, -1.3) * mm, "end": v(-75, -2) * mm});
            skLineSegment(sketch, "E284", {"start": v(-75, -2) * mm, "end": v(-75, -18.74) * mm});
            skArc(sketch, "E285", {"start": v(-75, -18.74) * mm, "mid": v(-74.7, -19.44) * mm, "end": v(-74, -19.74) * mm});
            skLineSegment(sketch, "E286", {"start": v(-74, -19.74) * mm, "end": v(-51.5, -19.74) * mm});
            skArc(sketch, "E287", {"start": v(-51.5, -19.74) * mm, "mid": v(-50.8, -19.44) * mm, "end": v(-50.5, -18.74) * mm});
            skLineSegment(sketch, "E288", {"start": v(-50.5, -39.47) * mm, "end": v(-50.5, -22.74) * mm});
            skArc(sketch, "E289", {"start": v(-50.5, -22.74) * mm, "mid": v(-50.8, -22.03) * mm, "end": v(-51.5, -21.74) * mm});
            skLineSegment(sketch, "E290", {"start": v(-51.5, -21.74) * mm, "end": v(-74, -21.74) * mm});
            skArc(sketch, "E291", {"start": v(-74, -21.74) * mm, "mid": v(-74.7, -22.03) * mm, "end": v(-75, -22.74) * mm});
            skLineSegment(sketch, "E292", {"start": v(-75, -22.74) * mm, "end": v(-75, -39.47) * mm});
            skArc(sketch, "E293", {"start": v(-75, -39.47) * mm, "mid": v(-74.7, -40.18) * mm, "end": v(-74, -40.47) * mm});
            skLineSegment(sketch, "E294", {"start": v(-74, -40.47) * mm, "end": v(-51.5, -40.47) * mm});
            skArc(sketch, "E295", {"start": v(-51.5, -40.47) * mm, "mid": v(-50.8, -40.18) * mm, "end": v(-50.5, -39.47) * mm});
            skLineSegment(sketch, "E296", {"start": v(-34.4, -51.5) * mm, "end": v(-34.4, -74) * mm});
            skArc(sketch, "E297", {"start": v(-34.4, -74) * mm, "mid": v(-34.12, -74.7) * mm, "end": v(-33.4, -75) * mm});
            skLineSegment(sketch, "E298", {"start": v(-33.4, -75) * mm, "end": v(-2, -75) * mm});
            skArc(sketch, "E299", {"start": v(-2, -75) * mm, "mid": v(-1.3, -74.7) * mm, "end": v(-1, -74) * mm});
            skLineSegment(sketch, "E300", {"start": v(-1, -74) * mm, "end": v(-1, -51.5) * mm});
            skArc(sketch, "E301", {"start": v(-1, -51.5) * mm, "mid": v(-1.3, -50.8) * mm, "end": v(-2, -50.5) * mm});
            skLineSegment(sketch, "E302", {"start": v(-2, -50.5) * mm, "end": v(-33.4, -50.5) * mm});
            skArc(sketch, "E303", {"start": v(-33.4, -50.5) * mm, "mid": v(-34.12, -50.8) * mm, "end": v(-34.4, -51.5) * mm});
            skLineSegment(sketch, "E304", {"start": v(-50.5, 18.73) * mm, "end": v(-50.5, 2) * mm});
            skArc(sketch, "E305", {"start": v(-51.5, 1) * mm, "mid": v(-50.8, 1.3) * mm, "end": v(-50.5, 2) * mm});
            skLineSegment(sketch, "E306", {"start": v(-51.5, 1) * mm, "end": v(-74, 1) * mm});
            skArc(sketch, "E307", {"start": v(-75, 2) * mm, "mid": v(-74.7, 1.3) * mm, "end": v(-74, 1) * mm});
            skLineSegment(sketch, "E308", {"start": v(-75, 2) * mm, "end": v(-75, 18.73) * mm});
            skArc(sketch, "E309", {"start": v(-74, 19.73) * mm, "mid": v(-74.7, 19.44) * mm, "end": v(-75, 18.73) * mm});
            skLineSegment(sketch, "E310", {"start": v(-74, 19.73) * mm, "end": v(-51.5, 19.73) * mm});
            skArc(sketch, "E311", {"start": v(-50.5, 18.73) * mm, "mid": v(-50.8, 19.44) * mm, "end": v(-51.5, 19.73) * mm});
            skLineSegment(sketch, "E312", {"start": v(-50.5, 39.47) * mm, "end": v(-50.5, 22.73) * mm});
            skArc(sketch, "E313", {"start": v(-51.5, 21.73) * mm, "mid": v(-50.8, 22.03) * mm, "end": v(-50.5, 22.73) * mm});
            skLineSegment(sketch, "E314", {"start": v(-51.5, 21.73) * mm, "end": v(-74, 21.73) * mm});
            skArc(sketch, "E315", {"start": v(-75, 22.73) * mm, "mid": v(-74.7, 22.03) * mm, "end": v(-74, 21.73) * mm});
            skLineSegment(sketch, "E316", {"start": v(-75, 22.73) * mm, "end": v(-75, 39.47) * mm});
            skArc(sketch, "E317", {"start": v(-74, 40.47) * mm, "mid": v(-74.7, 40.18) * mm, "end": v(-75, 39.47) * mm});
            skLineSegment(sketch, "E318", {"start": v(-74, 40.47) * mm, "end": v(-51.5, 40.47) * mm});
            skArc(sketch, "E319", {"start": v(-50.5, 39.47) * mm, "mid": v(-50.8, 40.18) * mm, "end": v(-51.5, 40.47) * mm});
            skLineSegment(sketch, "E320", {"start": v(-34.4, 51.5) * mm, "end": v(-34.4, 74) * mm});
            skArc(sketch, "E321", {"start": v(-33.4, 75) * mm, "mid": v(-34.12, 74.7) * mm, "end": v(-34.4, 74) * mm});
            skLineSegment(sketch, "E322", {"start": v(-33.4, 75) * mm, "end": v(-2, 75) * mm});
            skArc(sketch, "E323", {"start": v(-1, 74) * mm, "mid": v(-1.3, 74.7) * mm, "end": v(-2, 75) * mm});
            skLineSegment(sketch, "E324", {"start": v(-1, 74) * mm, "end": v(-1, 51.5) * mm});
            skArc(sketch, "E325", {"start": v(-2, 50.5) * mm, "mid": v(-1.3, 50.8) * mm, "end": v(-1, 51.5) * mm});
            skLineSegment(sketch, "E326", {"start": v(-2, 50.5) * mm, "end": v(-33.4, 50.5) * mm});
            skArc(sketch, "E327", {"start": v(-34.4, 51.5) * mm, "mid": v(-34.12, 50.8) * mm, "end": v(-33.4, 50.5) * mm});
            skLineSegment(sketch, "E328", {"start": v(50.5, -18.74) * mm, "end": v(50.5, -2) * mm});
            skArc(sketch, "E329", {"start": v(51.5, -1) * mm, "mid": v(50.8, -1.3) * mm, "end": v(50.5, -2) * mm});
            skLineSegment(sketch, "E330", {"start": v(51.5, -1) * mm, "end": v(74, -1) * mm});
            skArc(sketch, "E331", {"start": v(75, -2) * mm, "mid": v(74.7, -1.3) * mm, "end": v(74, -1) * mm});
            skLineSegment(sketch, "E332", {"start": v(75, -2) * mm, "end": v(75, -18.74) * mm});
            skArc(sketch, "E333", {"start": v(74, -19.74) * mm, "mid": v(74.7, -19.44) * mm, "end": v(75, -18.74) * mm});
            skLineSegment(sketch, "E334", {"start": v(74, -19.74) * mm, "end": v(51.5, -19.74) * mm});
            skArc(sketch, "E335", {"start": v(50.5, -18.74) * mm, "mid": v(50.8, -19.44) * mm, "end": v(51.5, -19.74) * mm});
            skLineSegment(sketch, "E336", {"start": v(50.5, -39.47) * mm, "end": v(50.5, -22.74) * mm});
            skArc(sketch, "E337", {"start": v(51.5, -21.74) * mm, "mid": v(50.8, -22.03) * mm, "end": v(50.5, -22.74) * mm});
            skLineSegment(sketch, "E338", {"start": v(51.5, -21.74) * mm, "end": v(74, -21.74) * mm});
            skArc(sketch, "E339", {"start": v(75, -22.74) * mm, "mid": v(74.7, -22.03) * mm, "end": v(74, -21.74) * mm});
            skLineSegment(sketch, "E340", {"start": v(75, -22.74) * mm, "end": v(75, -39.47) * mm});
            skArc(sketch, "E341", {"start": v(74, -40.47) * mm, "mid": v(74.7, -40.18) * mm, "end": v(75, -39.47) * mm});
            skLineSegment(sketch, "E342", {"start": v(74, -40.47) * mm, "end": v(51.5, -40.47) * mm});
            skArc(sketch, "E343", {"start": v(50.5, -39.47) * mm, "mid": v(50.8, -40.18) * mm, "end": v(51.5, -40.47) * mm});
            skLineSegment(sketch, "E344", {"start": v(34.4, -51.5) * mm, "end": v(34.4, -74) * mm});
            skArc(sketch, "E345", {"start": v(33.4, -75) * mm, "mid": v(34.12, -74.7) * mm, "end": v(34.4, -74) * mm});
            skLineSegment(sketch, "E346", {"start": v(33.4, -75) * mm, "end": v(2, -75) * mm});
            skArc(sketch, "E347", {"start": v(1, -74) * mm, "mid": v(1.3, -74.7) * mm, "end": v(2, -75) * mm});
            skLineSegment(sketch, "E348", {"start": v(1, -74) * mm, "end": v(1, -51.5) * mm});
            skArc(sketch, "E349", {"start": v(2, -50.5) * mm, "mid": v(1.3, -50.8) * mm, "end": v(1, -51.5) * mm});
            skLineSegment(sketch, "E350", {"start": v(2, -50.5) * mm, "end": v(33.4, -50.5) * mm});
            skArc(sketch, "E351", {"start": v(34.4, -51.5) * mm, "mid": v(34.12, -50.8) * mm, "end": v(33.4, -50.5) * mm});
            skLineSegment(sketch, "E352", {"start": v(50.5, 18.73) * mm, "end": v(50.5, 2) * mm});
            skArc(sketch, "E353", {"start": v(50.5, 2) * mm, "mid": v(50.8, 1.3) * mm, "end": v(51.5, 1) * mm});
            skLineSegment(sketch, "E354", {"start": v(51.5, 1) * mm, "end": v(74, 1) * mm});
            skArc(sketch, "E355", {"start": v(74, 1) * mm, "mid": v(74.7, 1.3) * mm, "end": v(75, 2) * mm});
            skLineSegment(sketch, "E356", {"start": v(75, 2) * mm, "end": v(75, 18.73) * mm});
            skArc(sketch, "E357", {"start": v(75, 18.73) * mm, "mid": v(74.7, 19.44) * mm, "end": v(74, 19.73) * mm});
            skLineSegment(sketch, "E358", {"start": v(74, 19.73) * mm, "end": v(51.5, 19.73) * mm});
            skArc(sketch, "E359", {"start": v(51.5, 19.73) * mm, "mid": v(50.8, 19.44) * mm, "end": v(50.5, 18.73) * mm});
            skLineSegment(sketch, "E360", {"start": v(50.5, 39.47) * mm, "end": v(50.5, 22.73) * mm});
            skArc(sketch, "E361", {"start": v(50.5, 22.73) * mm, "mid": v(50.8, 22.03) * mm, "end": v(51.5, 21.73) * mm});
            skLineSegment(sketch, "E362", {"start": v(51.5, 21.73) * mm, "end": v(74, 21.73) * mm});
            skArc(sketch, "E363", {"start": v(74, 21.73) * mm, "mid": v(74.7, 22.03) * mm, "end": v(75, 22.73) * mm});
            skLineSegment(sketch, "E364", {"start": v(75, 22.73) * mm, "end": v(75, 39.47) * mm});
            skArc(sketch, "E365", {"start": v(75, 39.47) * mm, "mid": v(74.7, 40.18) * mm, "end": v(74, 40.47) * mm});
            skLineSegment(sketch, "E366", {"start": v(74, 40.47) * mm, "end": v(51.5, 40.47) * mm});
            skArc(sketch, "E367", {"start": v(51.5, 40.47) * mm, "mid": v(50.8, 40.18) * mm, "end": v(50.5, 39.47) * mm});
            skLineSegment(sketch, "E368", {"start": v(34.4, 51.5) * mm, "end": v(34.4, 74) * mm});
            skArc(sketch, "E369", {"start": v(34.4, 74) * mm, "mid": v(34.12, 74.7) * mm, "end": v(33.4, 75) * mm});
            skLineSegment(sketch, "E370", {"start": v(33.4, 75) * mm, "end": v(2, 75) * mm});
            skArc(sketch, "E371", {"start": v(2, 75) * mm, "mid": v(1.3, 74.7) * mm, "end": v(1, 74) * mm});
            skLineSegment(sketch, "E372", {"start": v(1, 74) * mm, "end": v(1, 51.5) * mm});
            skArc(sketch, "E373", {"start": v(1, 51.5) * mm, "mid": v(1.3, 50.8) * mm, "end": v(2, 50.5) * mm});
            skLineSegment(sketch, "E374", {"start": v(2, 50.5) * mm, "end": v(33.4, 50.5) * mm});
            skArc(sketch, "E375", {"start": v(33.4, 50.5) * mm, "mid": v(34.12, 50.8) * mm, "end": v(34.4, 51.5) * mm});
            skLineSegment(sketch, "E376", {"start": v(-37.4, -75) * mm, "end": v(-74, -75) * mm});
            skLineSegment(sketch, "E377", {"start": v(-75, -74) * mm, "end": v(-75, -43.47) * mm});
            skLineSegment(sketch, "E378", {"start": v(-74, -42.47) * mm, "end": v(-51.5, -42.47) * mm});
            skLineSegment(sketch, "E379", {"start": v(-50.5, -43.47) * mm, "end": v(-50.5, -50.5) * mm});
            skLineSegment(sketch, "E380", {"start": v(-50.5, -50.5) * mm, "end": v(-37.4, -50.5) * mm});
            skLineSegment(sketch, "E381", {"start": v(-36.4, -51.5) * mm, "end": v(-36.4, -74) * mm});
            skArc(sketch, "E382", {"start": v(-75, -74) * mm, "mid": v(-74.7, -74.7) * mm, "end": v(-74, -75) * mm});
            skArc(sketch, "E383", {"start": v(-74, -42.47) * mm, "mid": v(-74.7, -42.76) * mm, "end": v(-75, -43.47) * mm});
            skArc(sketch, "E384", {"start": v(-50.5, -43.47) * mm, "mid": v(-50.8, -42.76) * mm, "end": v(-51.5, -42.47) * mm});
            skArc(sketch, "E385", {"start": v(-36.4, -51.5) * mm, "mid": v(-36.7, -50.8) * mm, "end": v(-37.4, -50.5) * mm});
            skArc(sketch, "E386", {"start": v(-37.4, -75) * mm, "mid": v(-36.7, -74.7) * mm, "end": v(-36.4, -74) * mm});
            skLineSegment(sketch, "E387", {"start": v(-37.4, 75) * mm, "end": v(-74, 75) * mm});
            skLineSegment(sketch, "E388", {"start": v(-75, 74) * mm, "end": v(-75, 43.47) * mm});
            skLineSegment(sketch, "E389", {"start": v(-74, 42.47) * mm, "end": v(-51.5, 42.47) * mm});
            skLineSegment(sketch, "E390", {"start": v(-50.5, 43.47) * mm, "end": v(-50.5, 50.5) * mm});
            skLineSegment(sketch, "E391", {"start": v(-50.5, 50.5) * mm, "end": v(-37.4, 50.5) * mm});
            skLineSegment(sketch, "E392", {"start": v(-36.4, 51.5) * mm, "end": v(-36.4, 74) * mm});
            skArc(sketch, "E393", {"start": v(-74, 75) * mm, "mid": v(-74.7, 74.7) * mm, "end": v(-75, 74) * mm});
            skArc(sketch, "E394", {"start": v(-75, 43.47) * mm, "mid": v(-74.7, 42.76) * mm, "end": v(-74, 42.47) * mm});
            skArc(sketch, "E395", {"start": v(-51.5, 42.47) * mm, "mid": v(-50.8, 42.76) * mm, "end": v(-50.5, 43.47) * mm});
            skArc(sketch, "E396", {"start": v(-37.4, 50.5) * mm, "mid": v(-36.7, 50.8) * mm, "end": v(-36.4, 51.5) * mm});
            skArc(sketch, "E397", {"start": v(-36.4, 74) * mm, "mid": v(-36.7, 74.7) * mm, "end": v(-37.4, 75) * mm});
            skLineSegment(sketch, "E398", {"start": v(37.4, -75) * mm, "end": v(74, -75) * mm});
            skLineSegment(sketch, "E399", {"start": v(75, -74) * mm, "end": v(75, -43.47) * mm});
            skLineSegment(sketch, "E400", {"start": v(74, -42.47) * mm, "end": v(51.5, -42.47) * mm});
            skLineSegment(sketch, "E401", {"start": v(50.5, -43.47) * mm, "end": v(50.5, -50.5) * mm});
            skLineSegment(sketch, "E402", {"start": v(50.5, -50.5) * mm, "end": v(37.4, -50.5) * mm});
            skLineSegment(sketch, "E403", {"start": v(36.4, -51.5) * mm, "end": v(36.4, -74) * mm});
            skArc(sketch, "E404", {"start": v(74, -75) * mm, "mid": v(74.7, -74.7) * mm, "end": v(75, -74) * mm});
            skArc(sketch, "E405", {"start": v(75, -43.47) * mm, "mid": v(74.7, -42.76) * mm, "end": v(74, -42.47) * mm});
            skArc(sketch, "E406", {"start": v(51.5, -42.47) * mm, "mid": v(50.8, -42.76) * mm, "end": v(50.5, -43.47) * mm});
            skArc(sketch, "E407", {"start": v(37.4, -50.5) * mm, "mid": v(36.7, -50.8) * mm, "end": v(36.4, -51.5) * mm});
            skArc(sketch, "E408", {"start": v(36.4, -74) * mm, "mid": v(36.7, -74.7) * mm, "end": v(37.4, -75) * mm});
            skLineSegment(sketch, "E409", {"start": v(37.4, 75) * mm, "end": v(74, 75) * mm});
            skLineSegment(sketch, "E410", {"start": v(75, 74) * mm, "end": v(75, 43.47) * mm});
            skLineSegment(sketch, "E411", {"start": v(74, 42.47) * mm, "end": v(51.5, 42.47) * mm});
            skLineSegment(sketch, "E412", {"start": v(50.5, 43.47) * mm, "end": v(50.5, 50.5) * mm});
            skLineSegment(sketch, "E413", {"start": v(50.5, 50.5) * mm, "end": v(37.4, 50.5) * mm});
            skLineSegment(sketch, "E414", {"start": v(36.4, 51.5) * mm, "end": v(36.4, 74) * mm});
            skArc(sketch, "E415", {"start": v(75, 74) * mm, "mid": v(74.7, 74.7) * mm, "end": v(74, 75) * mm});
            skArc(sketch, "E416", {"start": v(74, 42.47) * mm, "mid": v(74.7, 42.76) * mm, "end": v(75, 43.47) * mm});
            skArc(sketch, "E417", {"start": v(50.5, 43.47) * mm, "mid": v(50.8, 42.76) * mm, "end": v(51.5, 42.47) * mm});
            skArc(sketch, "E418", {"start": v(36.4, 51.5) * mm, "mid": v(36.7, 50.8) * mm, "end": v(37.4, 50.5) * mm});
            skArc(sketch, "E419", {"start": v(37.4, 75) * mm, "mid": v(36.7, 74.7) * mm, "end": v(36.4, 74) * mm});
            skSolve(sketch);
        }
        {
            var Q0;
            Q0=makeQuery(id+"F0.imprint","IMPRINT",FACE,{"disambiguationData":[TD([[makeQuery(id+"F0.imprint","IMPRINT",EDGE,{"derivedFrom":sQuery(id+"F0.wireOp",EDGE,"E4")}),-1.0]])]});
            extrude(context, id + "F1", {"entities" : qUnion([Q0]), "depth" : 7.5 * mm, "offsetDistance" : 25 * mm});
        }
        {
            var Q0;
            {var subQ5=sQuery(id+"F0.wireOp",EDGE,"E126");Q0=makeQuery(id+"F0.imprint","IMPRINT",FACE,{"disambiguationData":[TD([[makeQuery(id+"F0.imprint","IMPRINT",EDGE,{"derivedFrom":subQ5}),1.0]])]});}
            var Q1;
            {var subQ0=sQuery(id+"F0.wireOp",EDGE,"E85");Q1=makeQuery(id+"F0.imprint","IMPRINT",FACE,{"disambiguationData":[TD([[makeQuery(id+"F0.imprint","IMPRINT",EDGE,{"derivedFrom":subQ0}),1.0]])]});}
            var Q2;
            {var subQ0=sQuery(id+"F0.wireOp",EDGE,"E91");Q2=makeQuery(id+"F0.imprint","IMPRINT",FACE,{"disambiguationData":[TD([[makeQuery(id+"F0.imprint","IMPRINT",EDGE,{"derivedFrom":subQ0}),1.0]])]});}
            var Q3;
            {var subQ0=sQuery(id+"F0.wireOp",EDGE,"E97");Q3=makeQuery(id+"F0.imprint","IMPRINT",FACE,{"disambiguationData":[TD([[makeQuery(id+"F0.imprint","IMPRINT",EDGE,{"derivedFrom":subQ0}),1.0]])]});}
            var Q4;
            {var subQ0=sQuery(id+"F0.wireOp",EDGE,"E103");Q4=makeQuery(id+"F0.imprint","IMPRINT",FACE,{"disambiguationData":[TD([[makeQuery(id+"F0.imprint","IMPRINT",EDGE,{"derivedFrom":subQ0}),1.0]])]});}
            var Q5;
            {var subQ5=sQuery(id+"F0.wireOp",EDGE,"E109");Q5=makeQuery(id+"F0.imprint","IMPRINT",FACE,{"disambiguationData":[TD([[makeQuery(id+"F0.imprint","IMPRINT",EDGE,{"derivedFrom":subQ5}),1.0]])]});}
            var Q6;
            {var subQ0=sQuery(id+"F0.wireOp",EDGE,"E79");Q6=makeQuery(id+"F0.imprint","IMPRINT",FACE,{"disambiguationData":[TD([[makeQuery(id+"F0.imprint","IMPRINT",EDGE,{"derivedFrom":subQ0}),1.0]])]});}
            var Q7;
            Q7=makeQuery(id+"F0.imprint","IMPRINT",FACE,{"disambiguationData":[TD([[makeQuery(id+"F0.imprint","IMPRINT",EDGE,{"derivedFrom":sQuery(id+"F0.wireOp",EDGE,"E12")}),1.0]])]});
            var Q8;
            Q8=makeQuery(id+"F0.imprint","IMPRINT",FACE,{"disambiguationData":[TD([[makeQuery(id+"F0.imprint","IMPRINT",EDGE,{"derivedFrom":sQuery(id+"F0.wireOp",EDGE,"E28")}),1.0]])]});
            var Q9;
            Q9=makeQuery(id+"F0.imprint","IMPRINT",FACE,{"disambiguationData":[TD([[makeQuery(id+"F0.imprint","IMPRINT",EDGE,{"derivedFrom":sQuery(id+"F0.wireOp",EDGE,"E52")}),1.0]])]});
            var Q10;
            Q10=makeQuery(id+"F0.imprint","IMPRINT",FACE,{"disambiguationData":[TD([[makeQuery(id+"F0.imprint","IMPRINT",EDGE,{"derivedFrom":sQuery(id+"F0.wireOp",EDGE,"E4")}),1.0]])]});
            var Q11;
            {var subQ0=sQuery(id+"F0.wireOp",EDGE,"E120");Q11=makeQuery(id+"F0.imprint","IMPRINT",FACE,{"disambiguationData":[TD([[makeQuery(id+"F0.imprint","IMPRINT",EDGE,{"derivedFrom":subQ0}),1.0]])]});}
            var Q12;
            {var subQ0=sQuery(id+"F0.wireOp",EDGE,"E114");Q12=makeQuery(id+"F0.imprint","IMPRINT",FACE,{"disambiguationData":[TD([[makeQuery(id+"F0.imprint","IMPRINT",EDGE,{"derivedFrom":subQ0}),1.0]])]});}
            var Q13;
            Q13=makeQuery(id+"F0.imprint","IMPRINT",FACE,{"disambiguationData":[TD([[makeQuery(id+"F0.imprint","IMPRINT",EDGE,{"derivedFrom":sQuery(id+"F0.wireOp",EDGE,"E60")}),1.0]])]});
            var Q14;
            Q14=makeQuery(id+"F0.imprint","IMPRINT",FACE,{"disambiguationData":[TD([[makeQuery(id+"F0.imprint","IMPRINT",EDGE,{"derivedFrom":sQuery(id+"F0.wireOp",EDGE,"E44")}),1.0]])]});
            var Q15;
            Q15=makeQuery(id+"F0.imprint","IMPRINT",FACE,{"disambiguationData":[TD([[makeQuery(id+"F0.imprint","IMPRINT",EDGE,{"derivedFrom":sQuery(id+"F0.wireOp",EDGE,"E36")}),1.0]])]});
            var Q16;
            Q16=makeQuery(id+"F0.imprint","IMPRINT",FACE,{"disambiguationData":[TD([[makeQuery(id+"F0.imprint","IMPRINT",EDGE,{"derivedFrom":sQuery(id+"F0.wireOp",EDGE,"E20")}),1.0]])]});
            var Q17;
            {var subQ0=sQuery(id+"F0.wireOp",EDGE,"E73");Q17=makeQuery(id+"F0.imprint","IMPRINT",FACE,{"disambiguationData":[TD([[makeQuery(id+"F0.imprint","IMPRINT",EDGE,{"derivedFrom":subQ0}),1.0]])]});}
            var Q18;
            {var subQ5=sQuery(id+"F0.wireOp",EDGE,"E68");Q18=makeQuery(id+"F0.imprint","IMPRINT",FACE,{"disambiguationData":[TD([[makeQuery(id+"F0.imprint","IMPRINT",EDGE,{"derivedFrom":subQ5}),1.0]])]});}
            var Q19;
            {var subQ0=sQuery(id+"F0.wireOp",EDGE,"E154");Q19=makeQuery(id+"F0.imprint","IMPRINT",FACE,{"disambiguationData":[TD([[makeQuery(id+"F0.imprint","IMPRINT",EDGE,{"derivedFrom":subQ0}),1.0]])]});}
            var Q20;
            {var subQ0=sQuery(id+"F0.wireOp",EDGE,"E148");Q20=makeQuery(id+"F0.imprint","IMPRINT",FACE,{"disambiguationData":[TD([[makeQuery(id+"F0.imprint","IMPRINT",EDGE,{"derivedFrom":subQ0}),1.0]])]});}
            var Q21;
            {var subQ0=sQuery(id+"F0.wireOp",EDGE,"E142");Q21=makeQuery(id+"F0.imprint","IMPRINT",FACE,{"disambiguationData":[TD([[makeQuery(id+"F0.imprint","IMPRINT",EDGE,{"derivedFrom":subQ0}),1.0]])]});}
            var Q22;
            {var subQ0=sQuery(id+"F0.wireOp",EDGE,"E136");Q22=makeQuery(id+"F0.imprint","IMPRINT",FACE,{"disambiguationData":[TD([[makeQuery(id+"F0.imprint","IMPRINT",EDGE,{"derivedFrom":subQ0}),1.0]])]});}
            var Q23;
            {var subQ5=sQuery(id+"F0.wireOp",EDGE,"E131");Q23=makeQuery(id+"F0.imprint","IMPRINT",FACE,{"disambiguationData":[TD([[makeQuery(id+"F0.imprint","IMPRINT",EDGE,{"derivedFrom":subQ5}),1.0]])]});}
            var Q24;
            {var subQ3=sQuery(id+"F0.wireOp",EDGE,"E396");Q24=makeQuery(id+"F0.imprint","IMPRINT",FACE,{"disambiguationData":[TD([[makeQuery(id+"F0.imprint","IMPRINT",EDGE,{"derivedFrom":subQ3}),-1.0]])]});}
            var Q25;
            {var subQ3=sQuery(id+"F0.wireOp",EDGE,"E327");Q25=makeQuery(id+"F0.imprint","IMPRINT",FACE,{"disambiguationData":[TD([[makeQuery(id+"F0.imprint","IMPRINT",EDGE,{"derivedFrom":subQ3}),-1.0]])]});}
            var Q26;
            {var subQ3=sQuery(id+"F0.wireOp",EDGE,"E395");Q26=makeQuery(id+"F0.imprint","IMPRINT",FACE,{"disambiguationData":[TD([[makeQuery(id+"F0.imprint","IMPRINT",EDGE,{"derivedFrom":subQ3}),-1.0]])]});}
            var Q27;
            {var subQ3=sQuery(id+"F0.wireOp",EDGE,"E319");Q27=makeQuery(id+"F0.imprint","IMPRINT",FACE,{"disambiguationData":[TD([[makeQuery(id+"F0.imprint","IMPRINT",EDGE,{"derivedFrom":subQ3}),-1.0]])]});}
            var Q28;
            {var subQ3=sQuery(id+"F0.wireOp",EDGE,"E313");Q28=makeQuery(id+"F0.imprint","IMPRINT",FACE,{"disambiguationData":[TD([[makeQuery(id+"F0.imprint","IMPRINT",EDGE,{"derivedFrom":subQ3}),-1.0]])]});}
            var Q29;
            {var subQ3=sQuery(id+"F0.wireOp",EDGE,"E311");Q29=makeQuery(id+"F0.imprint","IMPRINT",FACE,{"disambiguationData":[TD([[makeQuery(id+"F0.imprint","IMPRINT",EDGE,{"derivedFrom":subQ3}),-1.0]])]});}
            var Q30;
            {var subQ3=sQuery(id+"F0.wireOp",EDGE,"E281");Q30=makeQuery(id+"F0.imprint","IMPRINT",FACE,{"disambiguationData":[TD([[makeQuery(id+"F0.imprint","IMPRINT",EDGE,{"derivedFrom":subQ3}),-1.0]])]});}
            var Q31;
            {var subQ3=sQuery(id+"F0.wireOp",EDGE,"E305");Q31=makeQuery(id+"F0.imprint","IMPRINT",FACE,{"disambiguationData":[TD([[makeQuery(id+"F0.imprint","IMPRINT",EDGE,{"derivedFrom":subQ3}),-1.0]])]});}
            var Q32;
            {var subQ3=sQuery(id+"F0.wireOp",EDGE,"E287");Q32=makeQuery(id+"F0.imprint","IMPRINT",FACE,{"disambiguationData":[TD([[makeQuery(id+"F0.imprint","IMPRINT",EDGE,{"derivedFrom":subQ3}),-1.0]])]});}
            var Q33;
            {var subQ3=sQuery(id+"F0.wireOp",EDGE,"E289");Q33=makeQuery(id+"F0.imprint","IMPRINT",FACE,{"disambiguationData":[TD([[makeQuery(id+"F0.imprint","IMPRINT",EDGE,{"derivedFrom":subQ3}),-1.0]])]});}
            var Q34;
            {var subQ3=sQuery(id+"F0.wireOp",EDGE,"E295");Q34=makeQuery(id+"F0.imprint","IMPRINT",FACE,{"disambiguationData":[TD([[makeQuery(id+"F0.imprint","IMPRINT",EDGE,{"derivedFrom":subQ3}),-1.0]])]});}
            var Q35;
            {var subQ3=sQuery(id+"F0.wireOp",EDGE,"E384");Q35=makeQuery(id+"F0.imprint","IMPRINT",FACE,{"disambiguationData":[TD([[makeQuery(id+"F0.imprint","IMPRINT",EDGE,{"derivedFrom":subQ3}),-1.0]])]});}
            var Q36;
            {var subQ3=sQuery(id+"F0.wireOp",EDGE,"E385");Q36=makeQuery(id+"F0.imprint","IMPRINT",FACE,{"disambiguationData":[TD([[makeQuery(id+"F0.imprint","IMPRINT",EDGE,{"derivedFrom":subQ3}),-1.0]])]});}
            var Q37;
            {var subQ3=sQuery(id+"F0.wireOp",EDGE,"E303");Q37=makeQuery(id+"F0.imprint","IMPRINT",FACE,{"disambiguationData":[TD([[makeQuery(id+"F0.imprint","IMPRINT",EDGE,{"derivedFrom":subQ3}),-1.0]])]});}
            var Q38;
            {var subQ3=sQuery(id+"F0.wireOp",EDGE,"E349");Q38=makeQuery(id+"F0.imprint","IMPRINT",FACE,{"disambiguationData":[TD([[makeQuery(id+"F0.imprint","IMPRINT",EDGE,{"derivedFrom":subQ3}),-1.0]])]});}
            var Q39;
            {var subQ3=sQuery(id+"F0.wireOp",EDGE,"E301");Q39=makeQuery(id+"F0.imprint","IMPRINT",FACE,{"disambiguationData":[TD([[makeQuery(id+"F0.imprint","IMPRINT",EDGE,{"derivedFrom":subQ3}),-1.0]])]});}
            var Q40;
            {var subQ3=sQuery(id+"F0.wireOp",EDGE,"E407");Q40=makeQuery(id+"F0.imprint","IMPRINT",FACE,{"disambiguationData":[TD([[makeQuery(id+"F0.imprint","IMPRINT",EDGE,{"derivedFrom":subQ3}),-1.0]])]});}
            var Q41;
            {var subQ3=sQuery(id+"F0.wireOp",EDGE,"E351");Q41=makeQuery(id+"F0.imprint","IMPRINT",FACE,{"disambiguationData":[TD([[makeQuery(id+"F0.imprint","IMPRINT",EDGE,{"derivedFrom":subQ3}),-1.0]])]});}
            var Q42;
            {var subQ3=sQuery(id+"F0.wireOp",EDGE,"E406");Q42=makeQuery(id+"F0.imprint","IMPRINT",FACE,{"disambiguationData":[TD([[makeQuery(id+"F0.imprint","IMPRINT",EDGE,{"derivedFrom":subQ3}),-1.0]])]});}
            var Q43;
            {var subQ3=sQuery(id+"F0.wireOp",EDGE,"E343");Q43=makeQuery(id+"F0.imprint","IMPRINT",FACE,{"disambiguationData":[TD([[makeQuery(id+"F0.imprint","IMPRINT",EDGE,{"derivedFrom":subQ3}),-1.0]])]});}
            var Q44;
            {var subQ3=sQuery(id+"F0.wireOp",EDGE,"E335");Q44=makeQuery(id+"F0.imprint","IMPRINT",FACE,{"disambiguationData":[TD([[makeQuery(id+"F0.imprint","IMPRINT",EDGE,{"derivedFrom":subQ3}),-1.0]])]});}
            var Q45;
            {var subQ3=sQuery(id+"F0.wireOp",EDGE,"E337");Q45=makeQuery(id+"F0.imprint","IMPRINT",FACE,{"disambiguationData":[TD([[makeQuery(id+"F0.imprint","IMPRINT",EDGE,{"derivedFrom":subQ3}),-1.0]])]});}
            var Q46;
            {var subQ3=sQuery(id+"F0.wireOp",EDGE,"E353");Q46=makeQuery(id+"F0.imprint","IMPRINT",FACE,{"disambiguationData":[TD([[makeQuery(id+"F0.imprint","IMPRINT",EDGE,{"derivedFrom":subQ3}),-1.0]])]});}
            var Q47;
            {var subQ3=sQuery(id+"F0.wireOp",EDGE,"E329");Q47=makeQuery(id+"F0.imprint","IMPRINT",FACE,{"disambiguationData":[TD([[makeQuery(id+"F0.imprint","IMPRINT",EDGE,{"derivedFrom":subQ3}),-1.0]])]});}
            var Q48;
            {var subQ3=sQuery(id+"F0.wireOp",EDGE,"E361");Q48=makeQuery(id+"F0.imprint","IMPRINT",FACE,{"disambiguationData":[TD([[makeQuery(id+"F0.imprint","IMPRINT",EDGE,{"derivedFrom":subQ3}),-1.0]])]});}
            var Q49;
            {var subQ3=sQuery(id+"F0.wireOp",EDGE,"E359");Q49=makeQuery(id+"F0.imprint","IMPRINT",FACE,{"disambiguationData":[TD([[makeQuery(id+"F0.imprint","IMPRINT",EDGE,{"derivedFrom":subQ3}),-1.0]])]});}
            var Q50;
            {var subQ3=sQuery(id+"F0.wireOp",EDGE,"E417");Q50=makeQuery(id+"F0.imprint","IMPRINT",FACE,{"disambiguationData":[TD([[makeQuery(id+"F0.imprint","IMPRINT",EDGE,{"derivedFrom":subQ3}),-1.0]])]});}
            var Q51;
            {var subQ3=sQuery(id+"F0.wireOp",EDGE,"E367");Q51=makeQuery(id+"F0.imprint","IMPRINT",FACE,{"disambiguationData":[TD([[makeQuery(id+"F0.imprint","IMPRINT",EDGE,{"derivedFrom":subQ3}),-1.0]])]});}
            var Q52;
            {var subQ3=sQuery(id+"F0.wireOp",EDGE,"E418");Q52=makeQuery(id+"F0.imprint","IMPRINT",FACE,{"disambiguationData":[TD([[makeQuery(id+"F0.imprint","IMPRINT",EDGE,{"derivedFrom":subQ3}),-1.0]])]});}
            var Q53;
            {var subQ3=sQuery(id+"F0.wireOp",EDGE,"E375");Q53=makeQuery(id+"F0.imprint","IMPRINT",FACE,{"disambiguationData":[TD([[makeQuery(id+"F0.imprint","IMPRINT",EDGE,{"derivedFrom":subQ3}),-1.0]])]});}
            var Q54;
            {var subQ3=sQuery(id+"F0.wireOp",EDGE,"E325");Q54=makeQuery(id+"F0.imprint","IMPRINT",FACE,{"disambiguationData":[TD([[makeQuery(id+"F0.imprint","IMPRINT",EDGE,{"derivedFrom":subQ3}),-1.0]])]});}
            var Q55;
            {var subQ3=sQuery(id+"F0.wireOp",EDGE,"E373");Q55=makeQuery(id+"F0.imprint","IMPRINT",FACE,{"disambiguationData":[TD([[makeQuery(id+"F0.imprint","IMPRINT",EDGE,{"derivedFrom":subQ3}),-1.0]])]});}
            extrude(context, id + "F2", {"entities" : qUnion([Q0, Q1, Q2, Q3, Q4, Q5, Q6, Q7, Q8, Q9, Q10, Q11, Q12, Q13, Q14, Q15, Q16, Q17, Q18, Q19, Q20, Q21, Q22, Q23, Q24, Q25, Q26, Q27, Q28, Q29, Q30, Q31, Q32, Q33, Q34, Q35, Q36, Q37, Q38, Q39, Q40, Q41, Q42, Q43, Q44, Q45, Q46, Q47, Q48, Q49, Q50, Q51, Q52, Q53, Q54, Q55]), "operationType" : NewBodyOperationType.ADD, "depth" : 7 * mm, "offsetDistance" : 25 * mm});
        }
        {
            var Q0;
            {var subQ7=sQuery(id+"F0.wireOp",EDGE,"E236");Q0=makeQuery(id+"F0.imprint","IMPRINT",FACE,{"disambiguationData":[TD([[makeQuery(id+"F0.imprint","IMPRINT",EDGE,{"derivedFrom":subQ7}),-1.0]])]});}
            var Q1;
            {var subQ3=sQuery(id+"F0.wireOp",EDGE,"E228");Q1=makeQuery(id+"F0.imprint","IMPRINT",FACE,{"disambiguationData":[TD([[makeQuery(id+"F0.imprint","IMPRINT",EDGE,{"derivedFrom":subQ3}),-1.0]])]});}
            var Q2;
            {var subQ3=sQuery(id+"F0.wireOp",EDGE,"E220");Q2=makeQuery(id+"F0.imprint","IMPRINT",FACE,{"disambiguationData":[TD([[makeQuery(id+"F0.imprint","IMPRINT",EDGE,{"derivedFrom":subQ3}),-1.0]])]});}
            var Q3;
            {var subQ5=sQuery(id+"F0.wireOp",EDGE,"E212");Q3=makeQuery(id+"F0.imprint","IMPRINT",FACE,{"disambiguationData":[TD([[makeQuery(id+"F0.imprint","IMPRINT",EDGE,{"derivedFrom":subQ5}),-1.0]])]});}
            var Q4;
            {var subQ3=sQuery(id+"F0.wireOp",EDGE,"E204");Q4=makeQuery(id+"F0.imprint","IMPRINT",FACE,{"disambiguationData":[TD([[makeQuery(id+"F0.imprint","IMPRINT",EDGE,{"derivedFrom":subQ3}),-1.0]])]});}
            var Q5;
            {var subQ8=sQuery(id+"F0.wireOp",EDGE,"E198");Q5=makeQuery(id+"F0.imprint","IMPRINT",FACE,{"disambiguationData":[TD([[makeQuery(id+"F0.imprint","IMPRINT",EDGE,{"derivedFrom":subQ8}),-1.0]])]});}
            var Q6;
            {var subQ1=sQuery(id+"F0.wireOp",EDGE,"E190");Q6=makeQuery(id+"F0.imprint","IMPRINT",FACE,{"disambiguationData":[TD([[makeQuery(id+"F0.imprint","IMPRINT",EDGE,{"derivedFrom":subQ1}),-1.0]])]});}
            var Q7;
            {var subQ4=sQuery(id+"F0.wireOp",EDGE,"E182");Q7=makeQuery(id+"F0.imprint","IMPRINT",FACE,{"disambiguationData":[TD([[makeQuery(id+"F0.imprint","IMPRINT",EDGE,{"derivedFrom":subQ4}),-1.0]])]});}
            var Q8;
            {var subQ7=sQuery(id+"F0.wireOp",EDGE,"E176");Q8=makeQuery(id+"F0.imprint","IMPRINT",FACE,{"disambiguationData":[TD([[makeQuery(id+"F0.imprint","IMPRINT",EDGE,{"derivedFrom":subQ7}),-1.0]])]});}
            var Q9;
            {var subQ5=sQuery(id+"F0.wireOp",EDGE,"E168");Q9=makeQuery(id+"F0.imprint","IMPRINT",FACE,{"disambiguationData":[TD([[makeQuery(id+"F0.imprint","IMPRINT",EDGE,{"derivedFrom":subQ5}),-1.0]])]});}
            var Q10;
            {var subQ4=sQuery(id+"F0.wireOp",EDGE,"E160");Q10=makeQuery(id+"F0.imprint","IMPRINT",FACE,{"disambiguationData":[TD([[makeQuery(id+"F0.imprint","IMPRINT",EDGE,{"derivedFrom":subQ4}),-1.0]])]});}
            var Q11;
            {var subQ3=sQuery(id+"F0.wireOp",EDGE,"E272");Q11=makeQuery(id+"F0.imprint","IMPRINT",FACE,{"disambiguationData":[TD([[makeQuery(id+"F0.imprint","IMPRINT",EDGE,{"derivedFrom":subQ3}),-1.0]])]});}
            var Q12;
            {var subQ4=sQuery(id+"F0.wireOp",EDGE,"E264");Q12=makeQuery(id+"F0.imprint","IMPRINT",FACE,{"disambiguationData":[TD([[makeQuery(id+"F0.imprint","IMPRINT",EDGE,{"derivedFrom":subQ4}),-1.0]])]});}
            var Q13;
            {var subQ2=sQuery(id+"F0.wireOp",EDGE,"E258");Q13=makeQuery(id+"F0.imprint","IMPRINT",FACE,{"disambiguationData":[TD([[makeQuery(id+"F0.imprint","IMPRINT",EDGE,{"derivedFrom":subQ2}),-1.0]])]});}
            var Q14;
            {var subQ4=sQuery(id+"F0.wireOp",EDGE,"E250");Q14=makeQuery(id+"F0.imprint","IMPRINT",FACE,{"disambiguationData":[TD([[makeQuery(id+"F0.imprint","IMPRINT",EDGE,{"derivedFrom":subQ4}),-1.0]])]});}
            var Q15;
            {var subQ4=sQuery(id+"F0.wireOp",EDGE,"E242");Q15=makeQuery(id+"F0.imprint","IMPRINT",FACE,{"disambiguationData":[TD([[makeQuery(id+"F0.imprint","IMPRINT",EDGE,{"derivedFrom":subQ4}),-1.0]])]});}
            var Q16;
            {var subQ3=sQuery(id+"F0.wireOp",EDGE,"E395");Q16=makeQuery(id+"F0.imprint","IMPRINT",FACE,{"disambiguationData":[TD([[makeQuery(id+"F0.imprint","IMPRINT",EDGE,{"derivedFrom":subQ3}),-1.0]])]});}
            var Q17;
            {var subQ3=sQuery(id+"F0.wireOp",EDGE,"E319");Q17=makeQuery(id+"F0.imprint","IMPRINT",FACE,{"disambiguationData":[TD([[makeQuery(id+"F0.imprint","IMPRINT",EDGE,{"derivedFrom":subQ3}),-1.0]])]});}
            var Q18;
            {var subQ3=sQuery(id+"F0.wireOp",EDGE,"E396");Q18=makeQuery(id+"F0.imprint","IMPRINT",FACE,{"disambiguationData":[TD([[makeQuery(id+"F0.imprint","IMPRINT",EDGE,{"derivedFrom":subQ3}),-1.0]])]});}
            var Q19;
            {var subQ3=sQuery(id+"F0.wireOp",EDGE,"E327");Q19=makeQuery(id+"F0.imprint","IMPRINT",FACE,{"disambiguationData":[TD([[makeQuery(id+"F0.imprint","IMPRINT",EDGE,{"derivedFrom":subQ3}),-1.0]])]});}
            var Q20;
            {var subQ3=sQuery(id+"F0.wireOp",EDGE,"E313");Q20=makeQuery(id+"F0.imprint","IMPRINT",FACE,{"disambiguationData":[TD([[makeQuery(id+"F0.imprint","IMPRINT",EDGE,{"derivedFrom":subQ3}),-1.0]])]});}
            var Q21;
            {var subQ3=sQuery(id+"F0.wireOp",EDGE,"E311");Q21=makeQuery(id+"F0.imprint","IMPRINT",FACE,{"disambiguationData":[TD([[makeQuery(id+"F0.imprint","IMPRINT",EDGE,{"derivedFrom":subQ3}),-1.0]])]});}
            var Q22;
            {var subQ3=sQuery(id+"F0.wireOp",EDGE,"E305");Q22=makeQuery(id+"F0.imprint","IMPRINT",FACE,{"disambiguationData":[TD([[makeQuery(id+"F0.imprint","IMPRINT",EDGE,{"derivedFrom":subQ3}),-1.0]])]});}
            var Q23;
            {var subQ3=sQuery(id+"F0.wireOp",EDGE,"E281");Q23=makeQuery(id+"F0.imprint","IMPRINT",FACE,{"disambiguationData":[TD([[makeQuery(id+"F0.imprint","IMPRINT",EDGE,{"derivedFrom":subQ3}),-1.0]])]});}
            var Q24;
            {var subQ3=sQuery(id+"F0.wireOp",EDGE,"E287");Q24=makeQuery(id+"F0.imprint","IMPRINT",FACE,{"disambiguationData":[TD([[makeQuery(id+"F0.imprint","IMPRINT",EDGE,{"derivedFrom":subQ3}),-1.0]])]});}
            var Q25;
            {var subQ3=sQuery(id+"F0.wireOp",EDGE,"E289");Q25=makeQuery(id+"F0.imprint","IMPRINT",FACE,{"disambiguationData":[TD([[makeQuery(id+"F0.imprint","IMPRINT",EDGE,{"derivedFrom":subQ3}),-1.0]])]});}
            var Q26;
            {var subQ3=sQuery(id+"F0.wireOp",EDGE,"E384");Q26=makeQuery(id+"F0.imprint","IMPRINT",FACE,{"disambiguationData":[TD([[makeQuery(id+"F0.imprint","IMPRINT",EDGE,{"derivedFrom":subQ3}),-1.0]])]});}
            var Q27;
            {var subQ3=sQuery(id+"F0.wireOp",EDGE,"E295");Q27=makeQuery(id+"F0.imprint","IMPRINT",FACE,{"disambiguationData":[TD([[makeQuery(id+"F0.imprint","IMPRINT",EDGE,{"derivedFrom":subQ3}),-1.0]])]});}
            var Q28;
            {var subQ3=sQuery(id+"F0.wireOp",EDGE,"E385");Q28=makeQuery(id+"F0.imprint","IMPRINT",FACE,{"disambiguationData":[TD([[makeQuery(id+"F0.imprint","IMPRINT",EDGE,{"derivedFrom":subQ3}),-1.0]])]});}
            var Q29;
            {var subQ3=sQuery(id+"F0.wireOp",EDGE,"E303");Q29=makeQuery(id+"F0.imprint","IMPRINT",FACE,{"disambiguationData":[TD([[makeQuery(id+"F0.imprint","IMPRINT",EDGE,{"derivedFrom":subQ3}),-1.0]])]});}
            var Q30;
            {var subQ3=sQuery(id+"F0.wireOp",EDGE,"E301");Q30=makeQuery(id+"F0.imprint","IMPRINT",FACE,{"disambiguationData":[TD([[makeQuery(id+"F0.imprint","IMPRINT",EDGE,{"derivedFrom":subQ3}),-1.0]])]});}
            var Q31;
            {var subQ3=sQuery(id+"F0.wireOp",EDGE,"E349");Q31=makeQuery(id+"F0.imprint","IMPRINT",FACE,{"disambiguationData":[TD([[makeQuery(id+"F0.imprint","IMPRINT",EDGE,{"derivedFrom":subQ3}),-1.0]])]});}
            var Q32;
            {var subQ3=sQuery(id+"F0.wireOp",EDGE,"E351");Q32=makeQuery(id+"F0.imprint","IMPRINT",FACE,{"disambiguationData":[TD([[makeQuery(id+"F0.imprint","IMPRINT",EDGE,{"derivedFrom":subQ3}),-1.0]])]});}
            var Q33;
            {var subQ3=sQuery(id+"F0.wireOp",EDGE,"E407");Q33=makeQuery(id+"F0.imprint","IMPRINT",FACE,{"disambiguationData":[TD([[makeQuery(id+"F0.imprint","IMPRINT",EDGE,{"derivedFrom":subQ3}),-1.0]])]});}
            var Q34;
            {var subQ3=sQuery(id+"F0.wireOp",EDGE,"E343");Q34=makeQuery(id+"F0.imprint","IMPRINT",FACE,{"disambiguationData":[TD([[makeQuery(id+"F0.imprint","IMPRINT",EDGE,{"derivedFrom":subQ3}),-1.0]])]});}
            var Q35;
            {var subQ3=sQuery(id+"F0.wireOp",EDGE,"E406");Q35=makeQuery(id+"F0.imprint","IMPRINT",FACE,{"disambiguationData":[TD([[makeQuery(id+"F0.imprint","IMPRINT",EDGE,{"derivedFrom":subQ3}),-1.0]])]});}
            var Q36;
            {var subQ3=sQuery(id+"F0.wireOp",EDGE,"E335");Q36=makeQuery(id+"F0.imprint","IMPRINT",FACE,{"disambiguationData":[TD([[makeQuery(id+"F0.imprint","IMPRINT",EDGE,{"derivedFrom":subQ3}),-1.0]])]});}
            var Q37;
            {var subQ3=sQuery(id+"F0.wireOp",EDGE,"E337");Q37=makeQuery(id+"F0.imprint","IMPRINT",FACE,{"disambiguationData":[TD([[makeQuery(id+"F0.imprint","IMPRINT",EDGE,{"derivedFrom":subQ3}),-1.0]])]});}
            var Q38;
            {var subQ3=sQuery(id+"F0.wireOp",EDGE,"E353");Q38=makeQuery(id+"F0.imprint","IMPRINT",FACE,{"disambiguationData":[TD([[makeQuery(id+"F0.imprint","IMPRINT",EDGE,{"derivedFrom":subQ3}),-1.0]])]});}
            var Q39;
            {var subQ3=sQuery(id+"F0.wireOp",EDGE,"E329");Q39=makeQuery(id+"F0.imprint","IMPRINT",FACE,{"disambiguationData":[TD([[makeQuery(id+"F0.imprint","IMPRINT",EDGE,{"derivedFrom":subQ3}),-1.0]])]});}
            var Q40;
            {var subQ3=sQuery(id+"F0.wireOp",EDGE,"E359");Q40=makeQuery(id+"F0.imprint","IMPRINT",FACE,{"disambiguationData":[TD([[makeQuery(id+"F0.imprint","IMPRINT",EDGE,{"derivedFrom":subQ3}),-1.0]])]});}
            var Q41;
            {var subQ3=sQuery(id+"F0.wireOp",EDGE,"E361");Q41=makeQuery(id+"F0.imprint","IMPRINT",FACE,{"disambiguationData":[TD([[makeQuery(id+"F0.imprint","IMPRINT",EDGE,{"derivedFrom":subQ3}),-1.0]])]});}
            var Q42;
            {var subQ3=sQuery(id+"F0.wireOp",EDGE,"E417");Q42=makeQuery(id+"F0.imprint","IMPRINT",FACE,{"disambiguationData":[TD([[makeQuery(id+"F0.imprint","IMPRINT",EDGE,{"derivedFrom":subQ3}),-1.0]])]});}
            var Q43;
            {var subQ3=sQuery(id+"F0.wireOp",EDGE,"E367");Q43=makeQuery(id+"F0.imprint","IMPRINT",FACE,{"disambiguationData":[TD([[makeQuery(id+"F0.imprint","IMPRINT",EDGE,{"derivedFrom":subQ3}),-1.0]])]});}
            var Q44;
            {var subQ3=sQuery(id+"F0.wireOp",EDGE,"E418");Q44=makeQuery(id+"F0.imprint","IMPRINT",FACE,{"disambiguationData":[TD([[makeQuery(id+"F0.imprint","IMPRINT",EDGE,{"derivedFrom":subQ3}),-1.0]])]});}
            var Q45;
            {var subQ3=sQuery(id+"F0.wireOp",EDGE,"E375");Q45=makeQuery(id+"F0.imprint","IMPRINT",FACE,{"disambiguationData":[TD([[makeQuery(id+"F0.imprint","IMPRINT",EDGE,{"derivedFrom":subQ3}),-1.0]])]});}
            var Q46;
            {var subQ3=sQuery(id+"F0.wireOp",EDGE,"E373");Q46=makeQuery(id+"F0.imprint","IMPRINT",FACE,{"disambiguationData":[TD([[makeQuery(id+"F0.imprint","IMPRINT",EDGE,{"derivedFrom":subQ3}),-1.0]])]});}
            var Q47;
            {var subQ3=sQuery(id+"F0.wireOp",EDGE,"E325");Q47=makeQuery(id+"F0.imprint","IMPRINT",FACE,{"disambiguationData":[TD([[makeQuery(id+"F0.imprint","IMPRINT",EDGE,{"derivedFrom":subQ3}),-1.0]])]});}
            extrude(context, id + "F3", {"entities" : qUnion([Q0, Q1, Q2, Q3, Q4, Q5, Q6, Q7, Q8, Q9, Q10, Q11, Q12, Q13, Q14, Q15, Q16, Q17, Q18, Q19, Q20, Q21, Q22, Q23, Q24, Q25, Q26, Q27, Q28, Q29, Q30, Q31, Q32, Q33, Q34, Q35, Q36, Q37, Q38, Q39, Q40, Q41, Q42, Q43, Q44, Q45, Q46, Q47]), "operationType" : NewBodyOperationType.ADD, "depth" : 5 * mm, "offsetDistance" : 25 * mm});
        }
        {
            var Q0;
            Q0=makeQuery(id+"F0.imprint","IMPRINT",FACE,{"disambiguationData":[TD([[makeQuery(id+"F0.imprint","IMPRINT",EDGE,{"derivedFrom":sQuery(id+"F0.wireOp",EDGE,"E0")}),-1.0]])]});
            extrude(context, id + "F4", {"entities" : qUnion([Q0]), "operationType" : NewBodyOperationType.ADD, "depth" : 8 * mm, "offsetDistance" : 25 * mm});
        }
    });
